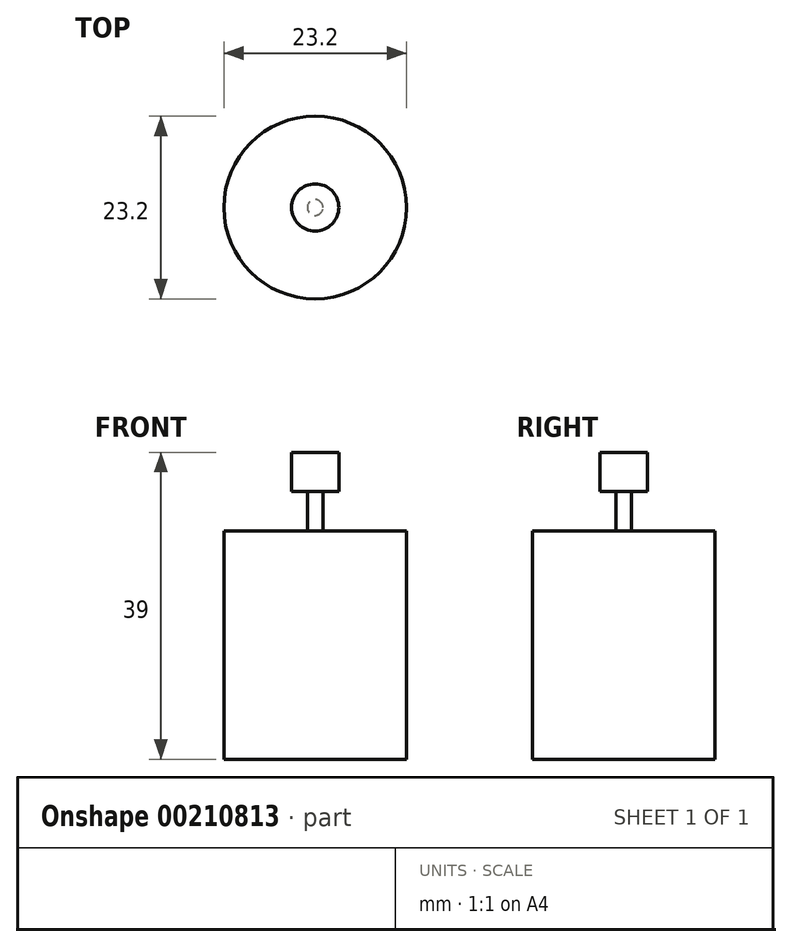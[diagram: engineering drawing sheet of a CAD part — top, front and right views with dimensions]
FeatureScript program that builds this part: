
annotation { "Feature Type Name" : "Feature", "Feature Type Description" : "" }
export const myFeature = defineFeature(function(context is Context, id is Id, definition is map)
    precondition{}
    {
        {
            var Q0;
            Q0=qCreatedBy(makeId("Top.planeOp"),FACE);
            var sketch = newSketch(context, id + "F0", { "sketchPlane" : qUnion([Q0])});
            skCircle(sketch, "E0", {"center": v(0, 0) * mm, "radius": 11.6 * mm});
            skSolve(sketch);
        }
        {
            var Q0;
            Q0=makeQuery(id+"F0.imprint","IMPRINT",FACE,{"disambiguationData":[TD([[makeQuery(id+"F0.imprint","IMPRINT",EDGE,{"derivedFrom":sQuery(id+"F0.wireOp",EDGE,"E0")}),1.0]])]});
            extrude(context, id + "F1", {"entities" : qUnion([Q0]), "depth" : 29 * mm});
        }
        {
            var Q0;
            Q0=makeQuery(id+"F1.opExtrude","CAP_FACE",FACE,{"disambiguationData":[OSD([sQuery(id+"F0.wireOp",EDGE,"E0")])],"isStart":false});
            var sketch = newSketch(context, id + "F2", { "sketchPlane" : qUnion([Q0])});
            skCircle(sketch, "E1", {"center": v(0, 0) * mm, "radius": 1 * mm});
            skSolve(sketch);
        }
        {
            var Q0;
            Q0=makeQuery(id+"F2.imprint","IMPRINT",FACE,{"disambiguationData":[TD([[makeQuery(id+"F2.imprint","IMPRINT",EDGE,{"derivedFrom":sQuery(id+"F2.wireOp",EDGE,"E1")}),1.0]])]});
            extrude(context, id + "F3", {"entities" : qUnion([Q0]), "operationType" : NewBodyOperationType.ADD, "depth" : 5 * mm});
        }
        {
            var Q0;
            Q0=makeQuery(id+"F3.opExtrude","CAP_FACE",FACE,{"disambiguationData":[OSD([sQuery(id+"F2.wireOp",EDGE,"E1")])],"isStart":false});
            var sketch = newSketch(context, id + "F4", { "sketchPlane" : qUnion([Q0])});
            skCircle(sketch, "E2", {"center": v(0, 0) * mm, "radius": 3 * mm});
            skSolve(sketch);
        }
        {
            var Q0;
            Q0=makeQuery(id+"F4.imprint","IMPRINT",FACE,{"disambiguationData":[TD([[makeQuery(id+"F4.imprint","IMPRINT",EDGE,{"derivedFrom":sQuery(id+"F4.wireOp",EDGE,"E2")}),1.0]])]});
            var Q1;
            Q1=makeQuery(id+"F4.imprint","IMPRINT",FACE,{"disambiguationData":[TD([[makeQuery(id+"F4.imprint","IMPRINT",EDGE,{"derivedFrom":makeQuery(id+"F3.opExtrude","CAP_EDGE",EDGE,{"disambiguationData":[OSD([sQuery(id+"F2.wireOp",EDGE,"E1")])],"isStart":false})}),1.0]])]});
            extrude(context, id + "F5", {"entities" : qUnion([Q0, Q1]), "depth" : 5 * mm});
        }
    });
